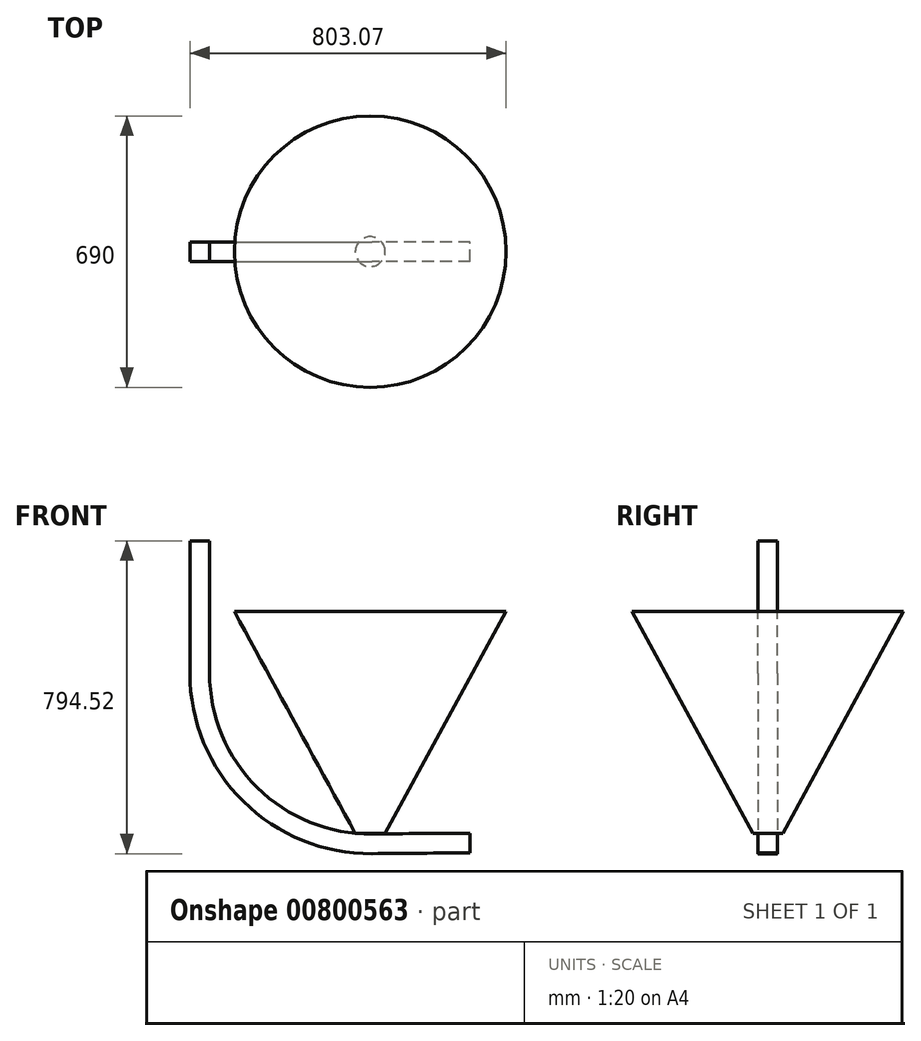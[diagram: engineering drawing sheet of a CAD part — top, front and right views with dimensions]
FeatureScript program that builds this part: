
annotation { "Feature Type Name" : "Feature", "Feature Type Description" : "" }
export const myFeature = defineFeature(function(context is Context, id is Id, definition is map)
    precondition{}
    {
        {
            var Q0;
            Q0=qCreatedBy(makeId("Right.planeOp"),FACE);
            var sketch = newSketch(context, id + "F0", { "sketchPlane" : qUnion([Q0])});
            skLineSegment(sketch, "E0", {"start": v(0, 0) * mm, "end": v(0, 563) * mm});
            skLineSegment(sketch, "E1", {"start": v(0, 563) * mm, "end": v(345, 563) * mm});
            skLineSegment(sketch, "E2", {"start": v(0, 0) * mm, "end": v(38, 0) * mm});
            skLineSegment(sketch, "E3", {"start": v(38, 0) * mm, "end": v(345, 563) * mm});
            skSolve(sketch);
        }
        {
            var Q0;
            Q0=makeQuery(id+"F0.imprint","IMPRINT",FACE,{"disambiguationData":[TD([[makeQuery(id+"F0.imprint","IMPRINT",EDGE,{"derivedFrom":sQuery(id+"F0.wireOp",EDGE,"E0")}),-1.0]])]});
            var Q1;
            Q1=sQuery(id+"F0.wireOp",EDGE,"E0");
            revolve(context, id + "F1", {"surfaceOperationType" : NewSurfaceOperationType.NEW, "entities" : qUnion([Q0]), "axis" : qUnion([Q1]), "revolveType" : RevolveType.FULL});
        }
        {
            var Q0;
            Q0=qCreatedBy(makeId("Front.planeOp"),FACE);
            var sketch = newSketch(context, id + "F2", { "sketchPlane" : qUnion([Q0])});
            skLineSegment(sketch, "E4", {"start": v(345, 563) * mm, "end": v(38, 0) * mm});
            skLineSegment(sketch, "E5", {"start": v(-38, 0) * mm, "end": v(-345, 563) * mm});
            skArc(sketch, "E6", {"start": v(-408.07, 406.3) * mm, "mid": v(-274.79, 104.61) * mm, "end": v(38, 0) * mm});
            skLineSegment(sketch, "E7", {"start": v(-408.07, 406.3) * mm, "end": v(-408.07, 742.75) * mm});
            skLineSegment(sketch, "E8", {"start": v(38, 0) * mm, "end": v(253.76, 0) * mm});
            skLineSegment(sketch, "E9.0", {"start": v(-458.07, 406.3) * mm, "end": v(-458.07, 742.75) * mm});
            skArc(sketch, "E9.1", {"start": v(-458.07, 406.3) * mm, "mid": v(-309.34, 68.46) * mm, "end": v(40.27, -50) * mm});
            skLineSegment(sketch, "E9.2", {"start": v(40.27, -50) * mm, "end": v(253.76, -50) * mm});
            skLineSegment(sketch, "E10", {"start": v(253.76, 0) * mm, "end": v(253.76, -50) * mm});
            skLineSegment(sketch, "E11", {"start": v(-408.07, 742.75) * mm, "end": v(-458.07, 742.75) * mm});
            skSolve(sketch);
        }
        {
            var Q0;
            {var subQ1=sQuery(id+"F2.wireOp",EDGE,"E7");Q0=makeQuery(id+"F2.imprint","IMPRINT",FACE,{"disambiguationData":[TD([[makeQuery(id+"F2.imprint","IMPRINT",EDGE,{"derivedFrom":subQ1}),1.0]])]});}
            extrude(context, id + "F3", {"entities" : qUnion([Q0]), "endBound" : BoundingType.SYMMETRIC, "depth" : 50 * mm, "offsetDistance" : 25.4 * mm});
        }
        {
            var Q0;
            Q0=makeQuery(id+"F3.opExtrude","SWEPT_EDGE",EDGE,{"disambiguationData":[OSD([sQuery(id+"F2.wireOp",EDGE,"E9.1"),sQuery(id+"F2.wireOp",EDGE,"E9.2")])]});
            fillet(context, id + "F4", {"entities" : qUnion([Q0]), "radius" : 48487.17 * mm, "tangentPropagation" : true, "allowEdgeOverflow" : false});
        }
        {
            var Q0;
            Q0=makeQuery(id+"F3.opExtrude","SWEPT_EDGE",EDGE,{"disambiguationData":[OSD([sQuery(id+"F2.wireOp",EDGE,"E6"),sQuery(id+"F2.wireOp",EDGE,"E8")])]});
            fillet(context, id + "F5", {"entities" : qUnion([Q0]), "radius" : 28480.05 * mm, "tangentPropagation" : true, "allowEdgeOverflow" : false});
        }
    });
